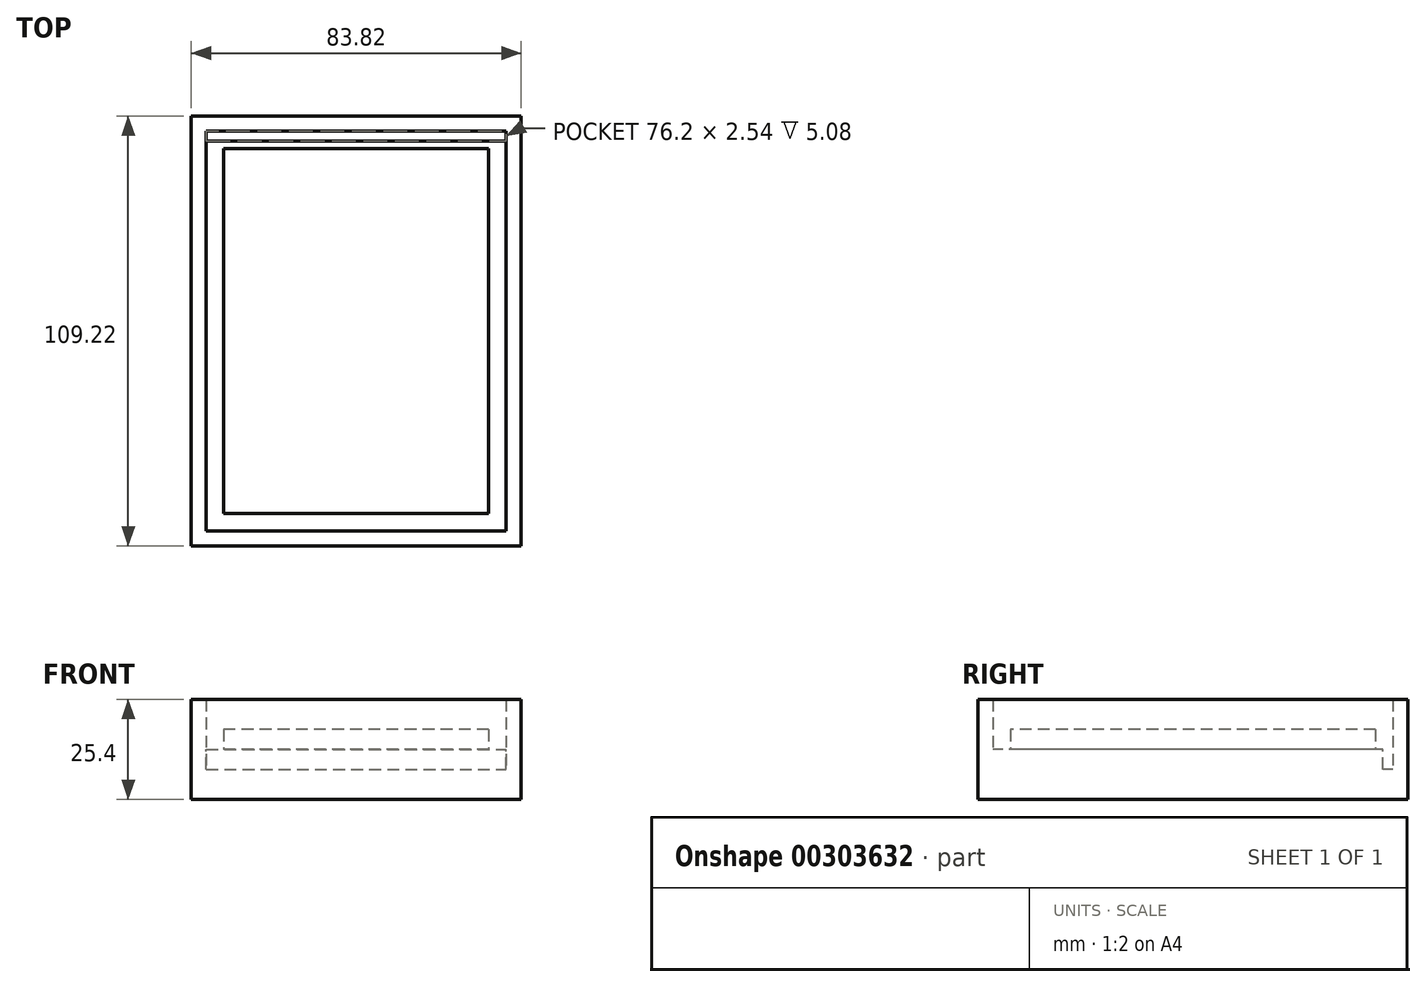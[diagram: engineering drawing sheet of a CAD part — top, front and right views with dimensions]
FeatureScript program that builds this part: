
annotation { "Feature Type Name" : "Feature", "Feature Type Description" : "" }
export const myFeature = defineFeature(function(context is Context, id is Id, definition is map)
    precondition{}
    {
        {
            var Q0;
            Q0=qCreatedBy(makeId("Top.planeOp"),FACE);
            var sketch = newSketch(context, id + "F0", { "sketchPlane" : qUnion([Q0])});
            skLineSegment(sketch, "E0.bottom", {"start": v(-41.9, 54.61) * mm, "end": v(41.91, 54.61) * mm});
            skLineSegment(sketch, "E0.top", {"start": v(-41.91, -54.61) * mm, "end": v(41.9, -54.61) * mm});
            skLineSegment(sketch, "E0.left", {"start": v(-41.9, 54.61) * mm, "end": v(-41.91, -54.61) * mm});
            skLineSegment(sketch, "E0.right", {"start": v(41.91, 54.61) * mm, "end": v(41.9, -54.61) * mm});
            skPoint(sketch, "E0.middle", {"position": v(0, 0) * mm});
            skLineSegment(sketch, "E1.bottom", {"start": v(-38.1, 50.8) * mm, "end": v(38.1, 50.8) * mm});
            skLineSegment(sketch, "E1.top", {"start": v(-38.1, -50.8) * mm, "end": v(38.1, -50.8) * mm});
            skLineSegment(sketch, "E1.left", {"start": v(-38.1, 50.8) * mm, "end": v(-38.1, -50.8) * mm});
            skLineSegment(sketch, "E1.right", {"start": v(38.1, 50.8) * mm, "end": v(38.1, -50.8) * mm});
            skSolve(sketch);
        }
        {
            var Q0;
            Q0=makeQuery(id+"F0.imprint","IMPRINT",FACE,{"disambiguationData":[TD([[makeQuery(id+"F0.imprint","IMPRINT",EDGE,{"derivedFrom":sQuery(id+"F0.wireOp",EDGE,"E1.bottom")}),-1.0]])]});
            extrude(context, id + "F1", {"entities" : qUnion([Q0]), "depth" : 12.7 * mm});
        }
        {
            var Q0;
            Q0 = qSketchRegion(id + "F0", true);
            extrude(context, id + "F2", {"entities" : qUnion([Q0]), "operationType" : NewBodyOperationType.ADD, "depth" : 25.4 * mm});
        }
        {
            var Q0;
            Q0=makeQuery(id+"F1.opExtrude","CAP_FACE",FACE,{"disambiguationData":[OSD([sQuery(id+"F0.wireOp",EDGE,"E1.bottom"),sQuery(id+"F0.wireOp",EDGE,"E1.top"),sQuery(id+"F0.wireOp",EDGE,"E1.left"),sQuery(id+"F0.wireOp",EDGE,"E1.right")])],"isStart":false});
            var sketch = newSketch(context, id + "F3", { "sketchPlane" : qUnion([Q0])});
            skLineSegment(sketch, "E2.bottom", {"start": v(33.65, 46.35) * mm, "end": v(-33.66, 46.35) * mm});
            skLineSegment(sketch, "E2.top", {"start": v(33.66, -46.36) * mm, "end": v(-33.66, -46.36) * mm});
            skLineSegment(sketch, "E2.left", {"start": v(33.65, 46.35) * mm, "end": v(33.66, -46.36) * mm});
            skLineSegment(sketch, "E2.right", {"start": v(-33.66, 46.35) * mm, "end": v(-33.65, -46.36) * mm});
            skPoint(sketch, "E2.middle", {"position": v(0, 0) * mm});
            skSolve(sketch);
        }
        {
            var Q0;
            Q0 = qSketchRegion(id + "F3", true);
            extrude(context, id + "F4", {"entities" : qUnion([Q0]), "operationType" : NewBodyOperationType.ADD, "depth" : 5.08 * mm});
        }
        {
            var Q0;
            Q0=makeQuery(id+"F1.opExtrude","CAP_FACE",FACE,{"disambiguationData":[OSD([sQuery(id+"F0.wireOp",EDGE,"E1.bottom"),sQuery(id+"F0.wireOp",EDGE,"E1.top"),sQuery(id+"F0.wireOp",EDGE,"E1.left"),sQuery(id+"F0.wireOp",EDGE,"E1.right")])],"isStart":false});
            var sketch = newSketch(context, id + "F5", { "sketchPlane" : qUnion([Q0])});
            skLineSegment(sketch, "E3.bottom", {"start": v(-38.1, 50.8) * mm, "end": v(38.1, 50.8) * mm});
            skLineSegment(sketch, "E3.top", {"start": v(-38.1, 48.26) * mm, "end": v(38.1, 48.26) * mm});
            skLineSegment(sketch, "E3.left", {"start": v(-38.1, 50.8) * mm, "end": v(-38.1, 48.26) * mm});
            skLineSegment(sketch, "E3.right", {"start": v(38.1, 50.8) * mm, "end": v(38.1, 48.26) * mm});
            skSolve(sketch);
        }
        {
            var Q0;
            Q0 = qSketchRegion(id + "F5", true);
            extrude(context, id + "F6", {"entities" : qUnion([Q0]), "operationType" : NewBodyOperationType.REMOVE, "oppositeDirection" : true, "depth" : 5.08 * mm});
        }
    });
